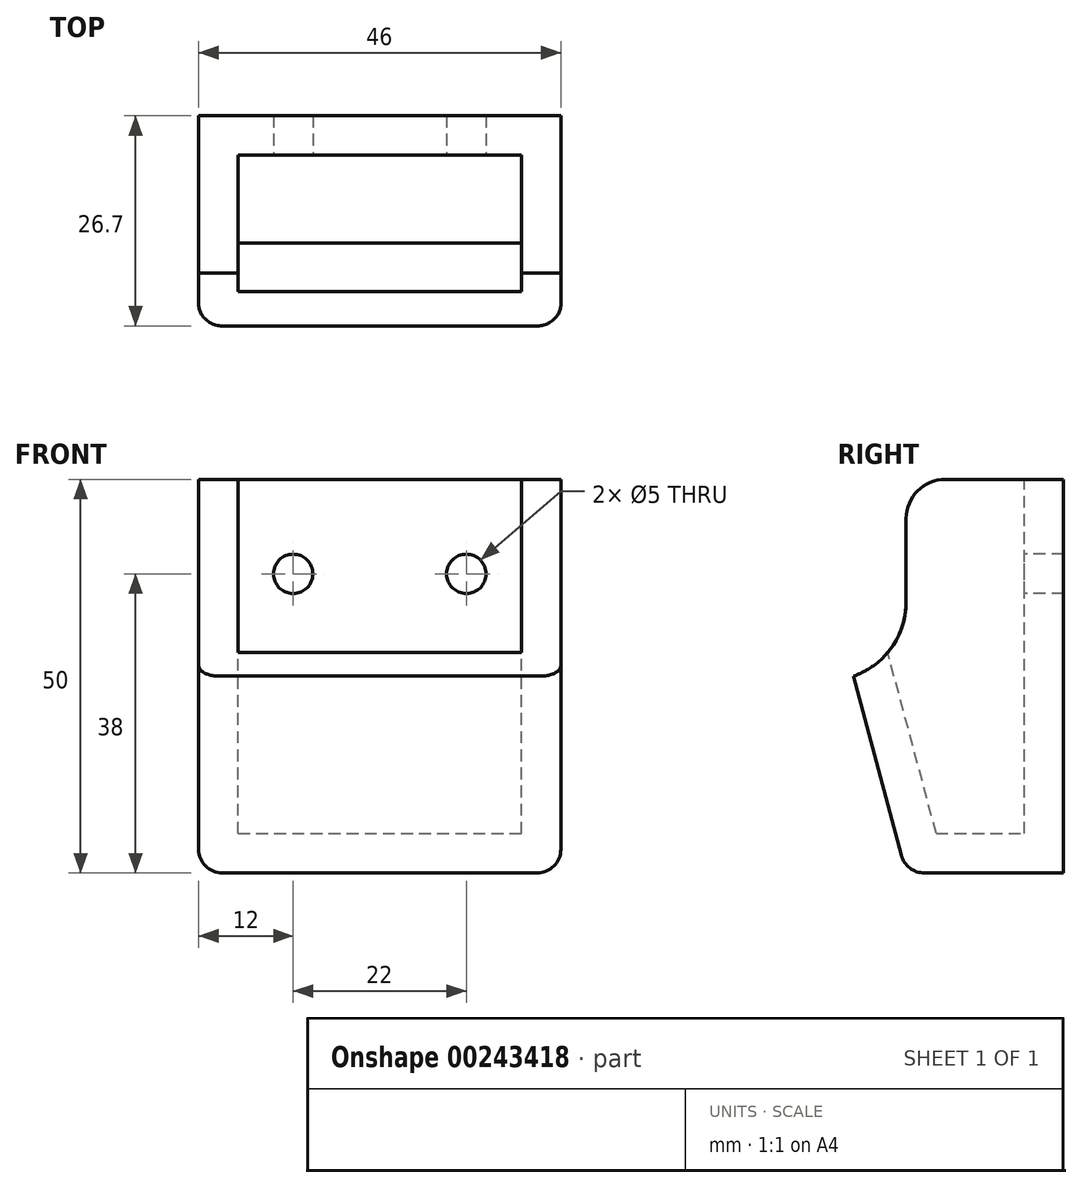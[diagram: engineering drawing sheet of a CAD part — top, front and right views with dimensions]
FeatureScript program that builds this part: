
annotation { "Feature Type Name" : "Feature", "Feature Type Description" : "" }
export const myFeature = defineFeature(function(context is Context, id is Id, definition is map)
    precondition{}
    {
        {
            var Q0;
            Q0=qCreatedBy(makeId("Right.planeOp"),FACE);
            var sketch = newSketch(context, id + "F0", { "sketchPlane" : qUnion([Q0])});
            skLineSegment(sketch, "E0", {"start": v(0, 0) * mm, "end": v(0, 50) * mm});
            skLineSegment(sketch, "E1", {"start": v(0, 0) * mm, "end": v(-20, 0) * mm});
            skLineSegment(sketch, "E2", {"start": v(-20, 0) * mm, "end": v(-26.7, 25) * mm});
            skLineSegment(sketch, "E3", {"start": v(-26.7, 25) * mm, "end": v(-20, 26.8) * mm});
            skLineSegment(sketch, "E4", {"start": v(-20, 26.8) * mm, "end": v(-20, 50) * mm});
            skLineSegment(sketch, "E5", {"start": v(-20, 50) * mm, "end": v(0, 50) * mm});
            skSolve(sketch);
        }
        {
            var Q0;
            Q0 = qSketchRegion(id + "F0", true);
            extrude(context, id + "F1", {"entities" : qUnion([Q0]), "oppositeDirection" : true, "depth" : 46 * mm, "symmetric" : true});
        }
        {
            var Q0;
            Q0=makeQuery(id+"F1.opExtrude","SWEPT_EDGE",EDGE,{"disambiguationData":[OSD([sQuery(id+"F0.wireOp",EDGE,"E3"),sQuery(id+"F0.wireOp",EDGE,"E4")])]});
            fillet(context, id + "F2", {"entities" : qUnion([Q0]), "radius" : 10 * mm, "tangentPropagation" : true, "allowEdgeOverflow" : false});
        }
        {
            var Q0;
            Q0=makeQuery(id+"F1.opExtrude","CAP_EDGE",EDGE,{"disambiguationData":[OSD([sQuery(id+"F0.wireOp",EDGE,"E2")])],"isStart":true});
            var Q1;
            Q1=makeQuery(id+"F1.opExtrude","SWEPT_EDGE",EDGE,{"disambiguationData":[OSD([sQuery(id+"F0.wireOp",EDGE,"E1"),sQuery(id+"F0.wireOp",EDGE,"E2")])]});
            var Q2;
            Q2=makeQuery(id+"F1.opExtrude","CAP_EDGE",EDGE,{"disambiguationData":[OSD([sQuery(id+"F0.wireOp",EDGE,"E2")])],"isStart":false});
            var Q3;
            Q3=makeQuery(id+"F1.opExtrude","CAP_EDGE",EDGE,{"disambiguationData":[OSD([sQuery(id+"F0.wireOp",EDGE,"E1")])],"isStart":true});
            var Q4;
            Q4=makeQuery(id+"F1.opExtrude","CAP_EDGE",EDGE,{"disambiguationData":[OSD([sQuery(id+"F0.wireOp",EDGE,"E1")])],"isStart":false});
            fillet(context, id + "F3", {"entities" : qUnion([Q0, Q1, Q2, Q3, Q4]), "radius" : 3 * mm, "tangentPropagation" : true, "allowEdgeOverflow" : false});
        }
        {
            var Q0;
            Q0=makeQuery(id+"F1.opExtrude","SWEPT_FACE",FACE,{"disambiguationData":[OSD([sQuery(id+"F0.wireOp",EDGE,"E5")])]});
            var Q1;
            Q1=makeQuery(id+"F1.opExtrude","SWEPT_FACE",FACE,{"disambiguationData":[OSD([sQuery(id+"F0.wireOp",EDGE,"E4")])]});
            var Q2;
            Q2=makeQuery(id+"F2.opFillet","BLEND_FACE",FACE,{"disambiguationData":[OSD([sQuery(id+"F0.wireOp",EDGE,"E3"),sQuery(id+"F0.wireOp",EDGE,"E4")])]});
            var Q3;
            Q3=makeQuery(id+"F1.opExtrude","SWEPT_FACE",FACE,{"disambiguationData":[OSD([sQuery(id+"F0.wireOp",EDGE,"E3")])]});
            shell(context, id + "F4", {"entities" : qUnion([Q0, Q1, Q2, Q3]), "thickness" : 5 * mm});
        }
        {
            var Q0;
            Q0=makeQuery(id+"F1.opExtrude","SWEPT_EDGE",EDGE,{"disambiguationData":[OSD([sQuery(id+"F0.wireOp",EDGE,"E4"),sQuery(id+"F0.wireOp",EDGE,"E5")])]});
            var Q1;
            Q1=makeQuery(id+"F4.opShell","OFFSET_EDGE",EDGE,{"disambiguationData":[OSD([sQuery(id+"F0.wireOp",EDGE,"E4"),sQuery(id+"F0.wireOp",EDGE,"E5")])]});
            fillet(context, id + "F5", {"entities" : qUnion([Q0, Q1]), "radius" : 5 * mm, "tangentPropagation" : true, "allowEdgeOverflow" : false});
        }
        {
            var Q0;
            Q0=makeQuery(id+"F4.opShell","OFFSET_FACE",FACE,{"disambiguationData":[OSD([sQuery(id+"F0.wireOp",EDGE,"E0")])]});
            var sketch = newSketch(context, id + "F6", { "sketchPlane" : qUnion([Q0])});
            skLineSegment(sketch, "E6", {"start": v(0, 50) * mm, "end": v(0, 38) * mm, "construction": true});
            skPoint(sketch, "E6.endSnap0", {"position": v(0, 50) * mm});
            skCircle(sketch, "E7", {"center": v(-11, 38) * mm, "radius": 2.5 * mm});
            skCircle(sketch, "E8", {"center": v(11, 38) * mm, "radius": 2.5 * mm});
            skLineSegment(sketch, "E9", {"start": v(-11, 38) * mm, "end": v(11, 38) * mm, "construction": true});
            skSolve(sketch);
        }
        {
            var Q0;
            Q0 = qSketchRegion(id + "F6", true);
            extrude(context, id + "F7", {"entities" : qUnion([Q0]), "operationType" : NewBodyOperationType.REMOVE, "oppositeDirection" : true, "depth" : 25 * mm});
        }
    });
